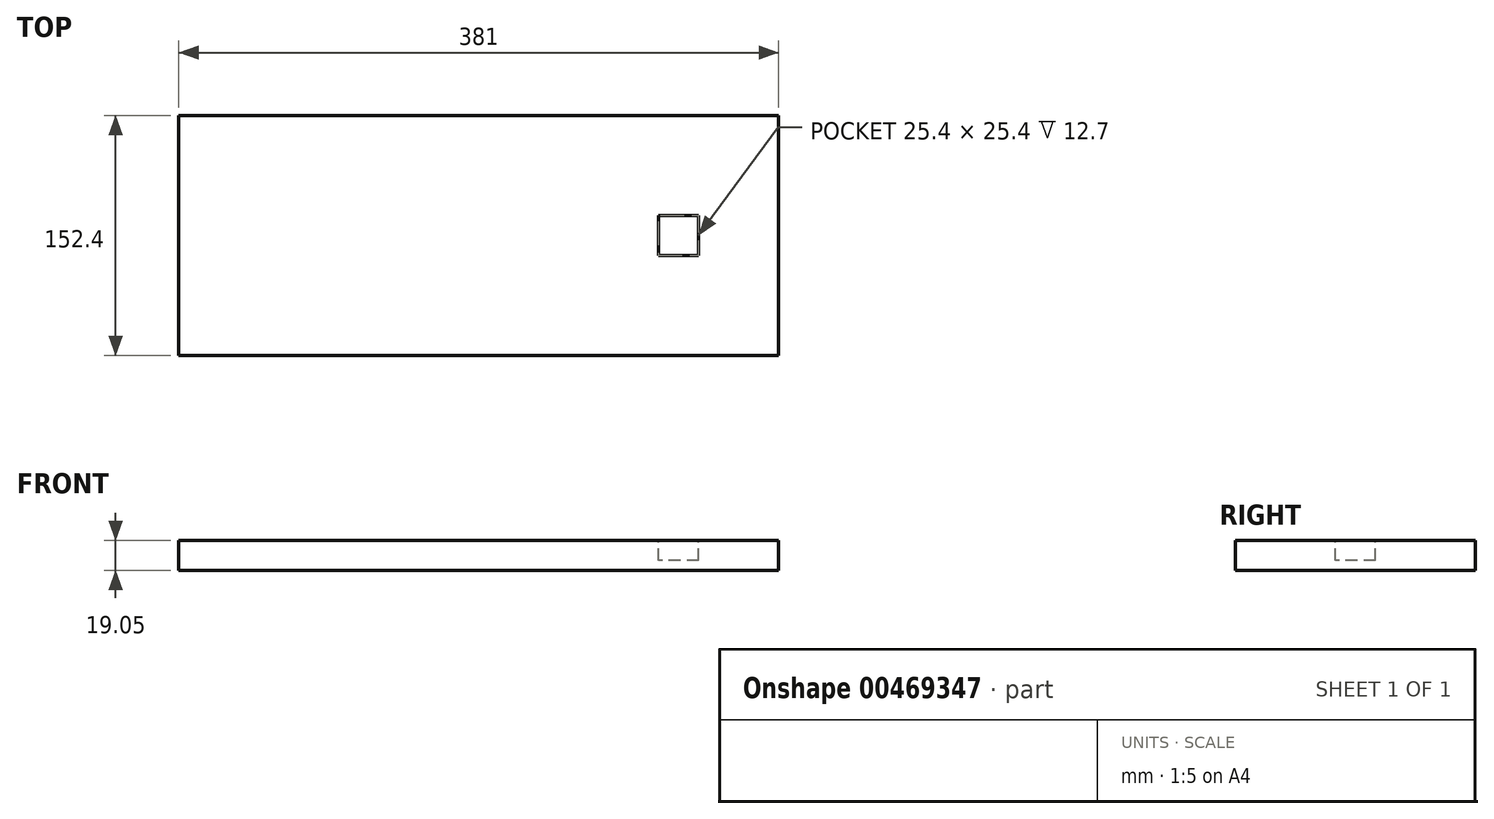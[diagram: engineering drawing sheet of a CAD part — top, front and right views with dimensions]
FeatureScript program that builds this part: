
annotation { "Feature Type Name" : "Feature", "Feature Type Description" : "" }
export const myFeature = defineFeature(function(context is Context, id is Id, definition is map)
    precondition{}
    {
        {
            var Q0;
            Q0=qCreatedBy(makeId("Top.planeOp"),FACE);
            var sketch = newSketch(context, id + "F0", { "sketchPlane" : qUnion([Q0])});
            skLineSegment(sketch, "E0.bottom", {"start": v(-190.5, 76.2) * mm, "end": v(190.5, 76.2) * mm});
            skLineSegment(sketch, "E0.top", {"start": v(-190.5, -76.2) * mm, "end": v(190.5, -76.2) * mm});
            skLineSegment(sketch, "E0.left", {"start": v(-190.5, 76.2) * mm, "end": v(-190.5, -76.2) * mm});
            skLineSegment(sketch, "E0.right", {"start": v(190.5, 76.2) * mm, "end": v(190.5, -76.2) * mm});
            skPoint(sketch, "E0.middle", {"position": v(0, 0) * mm});
            skSolve(sketch);
        }
        {
            var Q0;
            Q0 = qSketchRegion(id + "F0", true);
            extrude(context, id + "F1", {"entities" : qUnion([Q0]), "offsetDistance" : 25.4 * mm, "depth" : 19.05 * mm});
        }
        {
            var Q0;
            Q0=makeQuery(id+"F1.opExtrude","CAP_FACE",FACE,{"disambiguationData":[OSD([sQuery(id+"F0.wireOp",EDGE,"E0.bottom"),sQuery(id+"F0.wireOp",EDGE,"E0.top"),sQuery(id+"F0.wireOp",EDGE,"E0.left"),sQuery(id+"F0.wireOp",EDGE,"E0.right")])],"isStart":false});
            var sketch = newSketch(context, id + "F2", { "sketchPlane" : qUnion([Q0])});
            skLineSegment(sketch, "E1.bottom", {"start": v(139.7, 12.7) * mm, "end": v(114.3, 12.7) * mm});
            skLineSegment(sketch, "E1.top", {"start": v(139.7, -12.7) * mm, "end": v(114.3, -12.7) * mm});
            skLineSegment(sketch, "E1.left", {"start": v(139.7, 12.7) * mm, "end": v(139.7, -12.7) * mm});
            skLineSegment(sketch, "E1.right", {"start": v(114.3, 12.7) * mm, "end": v(114.3, -12.7) * mm});
            skPoint(sketch, "E1.middle", {"position": v(127, 0) * mm});
            skSolve(sketch);
        }
        {
            var Q0;
            Q0 = qSketchRegion(id + "F2", true);
            extrude(context, id + "F3", {"entities" : qUnion([Q0]), "operationType" : NewBodyOperationType.REMOVE, "oppositeDirection" : true, "depth" : 12.7 * mm});
        }
    });
